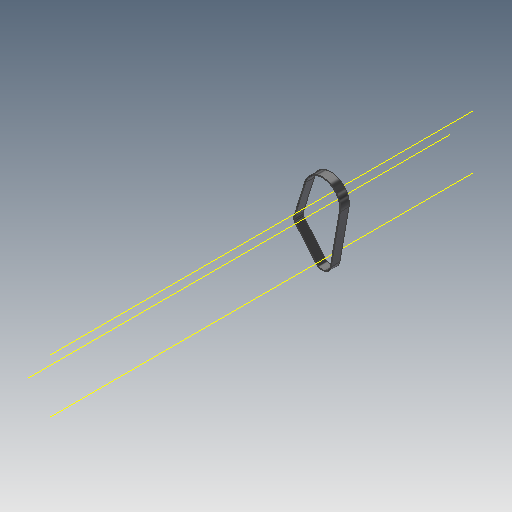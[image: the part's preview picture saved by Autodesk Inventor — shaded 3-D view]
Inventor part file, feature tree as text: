
AUTODESK INVENTOR PART (.ipt)
format: ipt  version: 2018 (Build 220112000, 112)  size: 108,032 bytes
history: native  units: mm (DEFAULTED — no unit token found)
features: other x5, plane x3, sketch x1, sweep x1
ambient origin geometry x8: Origin, YZ Plane, XZ Plane, XY Plane, X Axis, Y Axis, Z Axis, Center Point
bodies: Solid1 (feature_tree)
feature tree (10):
  sketch  "Sketch Path"  dims[d0=6.0mm d2=0.0mm d4=0.3mm d5=0.3mm d6=0.0mm d7=0.0mm d8=0.0mm d9=0.0mm d10=0.0mm d11=0.0mm d12=0.0mm d13=0.0mm]
  other  "Cross Section Plane"
  other  "Work Axis1"
  other  "Work Axis2"
  other  "Work Axis3"
  plane  "Work Plane2"
  plane  "Work Plane3"
  plane  "Work Plane4"
  sweep  "Belt"
  other  "Cross Section"
